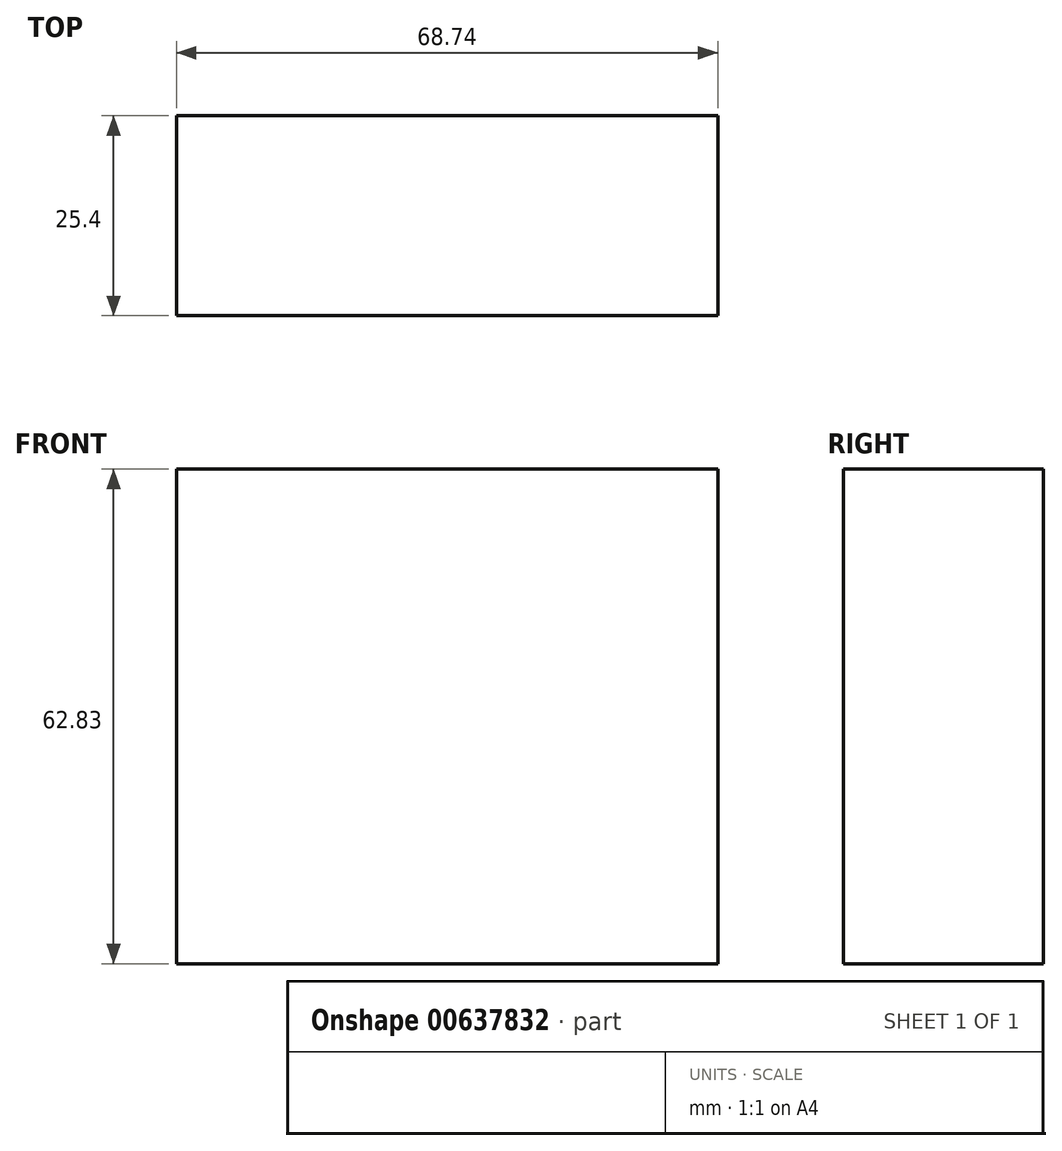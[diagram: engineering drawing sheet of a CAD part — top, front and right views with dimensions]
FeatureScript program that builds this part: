
annotation { "Feature Type Name" : "Feature", "Feature Type Description" : "" }
export const myFeature = defineFeature(function(context is Context, id is Id, definition is map)
    precondition{}
    {
        {
            var Q0;
            Q0=qCreatedBy(makeId("Front.planeOp"),FACE);
            var sketch = newSketch(context, id + "F0", { "sketchPlane" : qUnion([Q0])});
            skLineSegment(sketch, "E0.bottom", {"start": v(-35.42, 34.28) * mm, "end": v(33.32, 34.28) * mm});
            skLineSegment(sketch, "E0.top", {"start": v(-35.42, -28.55) * mm, "end": v(33.32, -28.55) * mm});
            skLineSegment(sketch, "E0.left", {"start": v(-35.42, 34.28) * mm, "end": v(-35.42, -28.55) * mm});
            skLineSegment(sketch, "E0.right", {"start": v(33.32, 34.28) * mm, "end": v(33.32, -28.55) * mm});
            skSolve(sketch);
        }
        {
            var Q0;
            Q0 = qSketchRegion(id + "F0", true);
            extrude(context, id + "F1", {"entities" : qUnion([Q0]), "depth" : 25.4 * mm, "offsetDistance" : 25.4 * mm});
        }
    });
